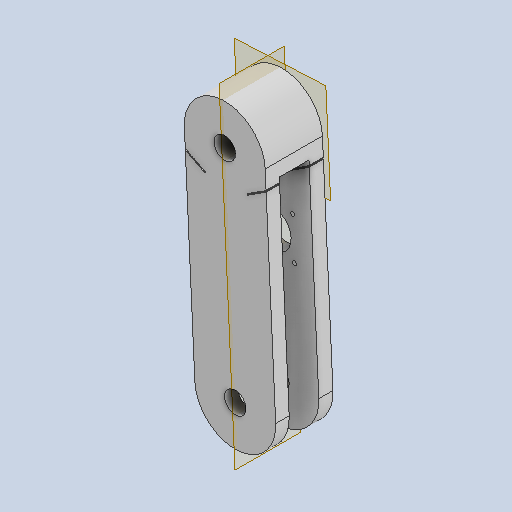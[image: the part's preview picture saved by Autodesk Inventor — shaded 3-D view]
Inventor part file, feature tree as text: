
AUTODESK INVENTOR PART (.ipt)
format: ipt  version: 2024 (Build 280153000, 153)  size: 698,368 bytes
history: native  units: mm
features: sketch x4, extrude x4, other x4, plane x3, projected_geometry x1, reference x1
ambient origin geometry x8: Origin, YZ Plane, XZ Plane, XY Plane, X Axis, Y Axis, Z Axis, Center Point
bodies: Solid1 (feature_tree)
feature tree (17):
  plane  "Work Plane1"
  sketch  "Sketch1"  dims[d0=10.0mm d1=0.0mm d2=160.0mm]
  plane  "Work Plane2"
  extrude  "Extrusion1"  Depth=10.0mm
  extrude  "Extrusion2"  TaperAngle=0.0deg  [1 undecoded]
  plane  "Work Plane3"
  extrude  "Extrusion3"  TaperAngle=0.0deg  [1 undecoded]
  extrude  "Extrusion4"  Depth=10.0mm
  sketch  "Sketch3"  dims[d3=10.0mm d4=0.0mm d5=0.0mm]
  projected_geometry  "Projected Loop1"
  sketch  "Sketch4"  dims[d6=3.0mm d7=0.0mm d8=0.0mm]
  reference  "Reference2"
  sketch  "Sketch6"  dims[d9=10.0mm d10=0.0mm d11=0.5mm d12=0.872665mm]
  other  "<userpath>\Documents\Inventor\robot arm\base.iam"
  other  "base.iam"
  other  "stepper motor:2"
  other  "bottom arm"
note: 2 required parameter values undecoded (feature->parameter linkage not recoverable at this tier; creation-order binding heuristic only, values carry confidence <= 0.55)
